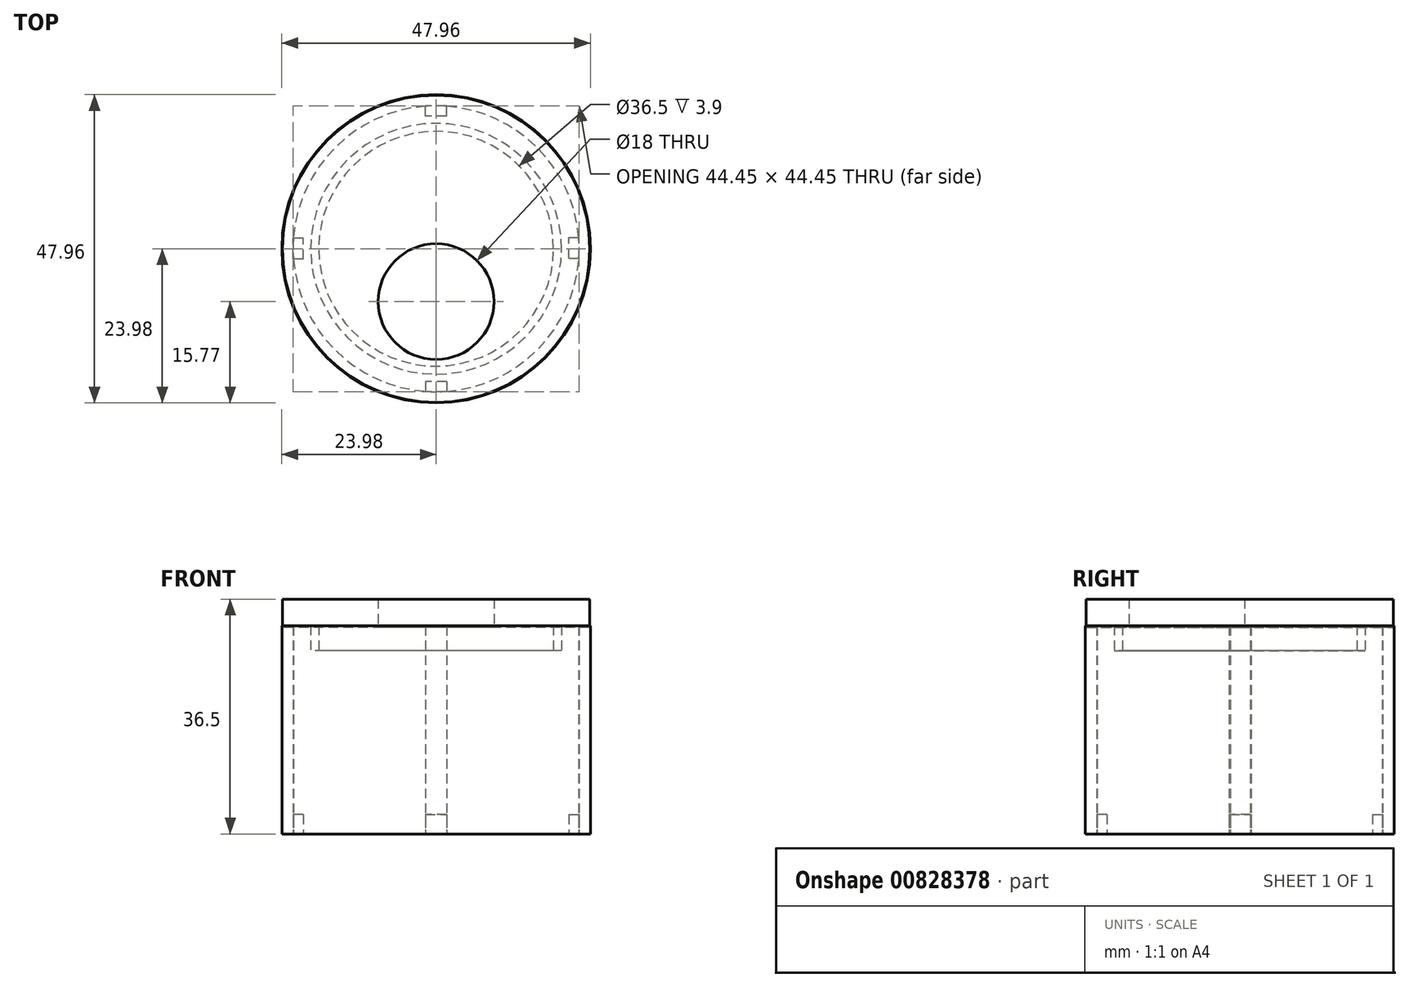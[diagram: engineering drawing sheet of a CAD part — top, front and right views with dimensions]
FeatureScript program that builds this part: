
annotation { "Feature Type Name" : "Feature", "Feature Type Description" : "" }
export const myFeature = defineFeature(function(context is Context, id is Id, definition is map)
    precondition{}
    {
        {
            var Q0;
            Q0=qCreatedBy(makeId("Top.planeOp"),FACE);
            var sketch = newSketch(context, id + "F0", { "sketchPlane" : qUnion([Q0])});
            skCircle(sketch, "E0", {"center": v(0, 0) * mm, "radius": 22.23 * mm});
            skCircle(sketch, "E1.0", {"center": v(0, 0) * mm, "radius": 23.98 * mm});
            skLineSegment(sketch, "E2.bottom", {"start": v(-20.62, -1.63) * mm, "end": v(-22.23, -1.63) * mm});
            skLineSegment(sketch, "E2.top", {"start": v(-20.62, 1.62) * mm, "end": v(-22.23, 1.62) * mm});
            skLineSegment(sketch, "E2.left", {"start": v(-20.62, -1.63) * mm, "end": v(-20.62, 1.63) * mm});
            skLineSegment(sketch, "E2.right", {"start": v(-22.23, -1.63) * mm, "end": v(-22.23, 1.62) * mm});
            skPoint(sketch, "E2.middle", {"position": v(-20.62, 0) * mm});
            skLineSegment(sketch, "E3.bottom", {"start": v(1.62, -20.62) * mm, "end": v(-1.62, -20.62) * mm});
            skLineSegment(sketch, "E3.top", {"start": v(1.62, -22.23) * mm, "end": v(-1.62, -22.23) * mm});
            skLineSegment(sketch, "E3.left", {"start": v(1.63, -20.62) * mm, "end": v(1.63, -22.23) * mm});
            skLineSegment(sketch, "E3.right", {"start": v(-1.62, -20.62) * mm, "end": v(-1.62, -22.23) * mm});
            skPoint(sketch, "E3.middle", {"position": v(0, -20.62) * mm});
            skLineSegment(sketch, "E4.bottom", {"start": v(20.62, -1.5) * mm, "end": v(22.23, -1.5) * mm});
            skLineSegment(sketch, "E4.top", {"start": v(20.62, 1.76) * mm, "end": v(22.23, 1.76) * mm});
            skLineSegment(sketch, "E4.left", {"start": v(20.62, -1.5) * mm, "end": v(20.62, 1.76) * mm});
            skLineSegment(sketch, "E4.right", {"start": v(22.23, -1.5) * mm, "end": v(22.23, 1.76) * mm});
            skPoint(sketch, "E4.middle", {"position": v(20.62, 0.13) * mm});
            skLineSegment(sketch, "E5.bottom", {"start": v(1.62, 20.62) * mm, "end": v(-1.63, 20.62) * mm});
            skLineSegment(sketch, "E5.top", {"start": v(1.62, 22.23) * mm, "end": v(-1.63, 22.23) * mm});
            skLineSegment(sketch, "E5.left", {"start": v(1.62, 20.62) * mm, "end": v(1.62, 22.23) * mm});
            skLineSegment(sketch, "E5.right", {"start": v(-1.63, 20.62) * mm, "end": v(-1.63, 22.23) * mm});
            skPoint(sketch, "E5.middle", {"position": v(0, 20.62) * mm});
            skCircle(sketch, "E6", {"center": v(0, 0) * mm, "radius": 19.5 * mm});
            skCircle(sketch, "E7.0", {"center": v(0, 0) * mm, "radius": 18.25 * mm});
            skSolve(sketch);
        }
        {
            var Q0;
            Q0=makeQuery(id+"F0.imprint","IMPRINT",FACE,{"disambiguationData":[TD([[makeQuery(id+"F0.imprint","IMPRINT",EDGE,{"derivedFrom":sQuery(id+"F0.wireOp",EDGE,"E1.0")}),1.0]])]});
            extrude(context, id + "F1", {"entities" : qUnion([Q0]), "depth" : 32.35 * mm, "offsetDistance" : 25 * mm});
        }
        {
            var Q0;
            {var subQ0=sQuery(id+"F0.wireOp",EDGE,"E5.bottom");Q0=makeQuery(id+"F0.imprint","IMPRINT",FACE,{"disambiguationData":[TD([[makeQuery(id+"F0.imprint","IMPRINT",EDGE,{"derivedFrom":subQ0}),-1.0]])]});}
            var Q1;
            {var subQ0=sQuery(id+"F0.wireOp",EDGE,"E4.left");Q1=makeQuery(id+"F0.imprint","IMPRINT",FACE,{"disambiguationData":[TD([[makeQuery(id+"F0.imprint","IMPRINT",EDGE,{"derivedFrom":subQ0}),-1.0]])]});}
            var Q2;
            {var subQ0=sQuery(id+"F0.wireOp",EDGE,"E3.bottom");Q2=makeQuery(id+"F0.imprint","IMPRINT",FACE,{"disambiguationData":[TD([[makeQuery(id+"F0.imprint","IMPRINT",EDGE,{"derivedFrom":subQ0}),1.0]])]});}
            var Q3;
            {var subQ0=sQuery(id+"F0.wireOp",EDGE,"E2.left");Q3=makeQuery(id+"F0.imprint","IMPRINT",FACE,{"disambiguationData":[TD([[makeQuery(id+"F0.imprint","IMPRINT",EDGE,{"derivedFrom":subQ0}),1.0]])]});}
            extrude(context, id + "F2", {"entities" : qUnion([Q0, Q1, Q2, Q3]), "operationType" : NewBodyOperationType.ADD, "depth" : 3 * mm, "offsetDistance" : 25 * mm});
        }
        {
            var Q0;
            Q0=makeQuery(id+"F0.imprint","IMPRINT",FACE,{"disambiguationData":[TD([[makeQuery(id+"F0.imprint","IMPRINT",EDGE,{"derivedFrom":sQuery(id+"F0.wireOp",EDGE,"E6")}),1.0]])]});
            extrude(context, id + "F3", {"entities" : qUnion([Q0]), "depth" : 32.4 * mm, "offsetDistance" : 25 * mm, "hasSecondDirection" : true, "secondDirectionOppositeDirection" : false, "secondDirectionDepth" : 28.5 * mm});
        }
        {
            var Q0;
            Q0=qCreatedBy(makeId("Top.planeOp"),FACE);
            var sketch = newSketch(context, id + "F4", { "sketchPlane" : qUnion([Q0])});
            skCircle(sketch, "E8", {"center": v(0, 0) * mm, "radius": 23.9 * mm});
            skSolve(sketch);
        }
        {
            var Q0;
            Q0 = qSketchRegion(id + "F4", true);
            extrude(context, id + "F5", {"entities" : qUnion([Q0]), "depth" : 36.5 * mm, "offsetDistance" : 25 * mm, "hasSecondDirection" : true, "secondDirectionOppositeDirection" : false, "secondDirectionDepth" : 32.1 * mm});
        }
        {
            var Q0;
            Q0=qCreatedBy(makeId("Top.planeOp"),FACE);
            var sketch = newSketch(context, id + "F6", { "sketchPlane" : qUnion([Q0])});
            skCircle(sketch, "E9", {"center": v(0, -8.2) * mm, "radius": 8.38 * mm});
            skSolve(sketch);
        }
        {
            var Q0;
            Q0=sQuery(id+"F6.wireOp",VERTEX,"E9.center");
            var Q1;
            Q1=makeQuery(id+"F5.opExtrude","SWEPT_BODY",BODY,{"disambiguationData":[OSD([sQuery(id+"F4.wireOp",EDGE,"E8")])]});
            hole(context, id + "F7", {"style" : HoleStyle.SIMPLE, "endStyle" : HoleEndStyle.THROUGH, "oppositeDirection" : true, "holeDiameter" : 18 * mm, "majorDiameter" : 5 * mm, "isTappedThrough" : true, "tappedDepth" : 12 * mm, "tapClearance" : 3, "locations" : qUnion([Q0]), "scope" : qUnion([Q1])});
        }
        {
            var Q0;
            Q0=qCreatedBy(makeId("Top.planeOp"),FACE);
            cPlane(context, id + "F8", {"entities" : qUnion([Q0]), "cplaneType" : CPlaneType.OFFSET, "offset" : 36.4 * mm, "width" : 150 * mm, "height" : 150 * mm});
        }
        {
            var Q0;
            Q0=qCreatedBy(id+"F8.planeOp",FACE);
            cPlane(context, id + "F9", {"entities" : qUnion([Q0]), "cplaneType" : CPlaneType.OFFSET, "offset" : 15 * mm, "width" : 150 * mm, "height" : 150 * mm});
        }
    });
